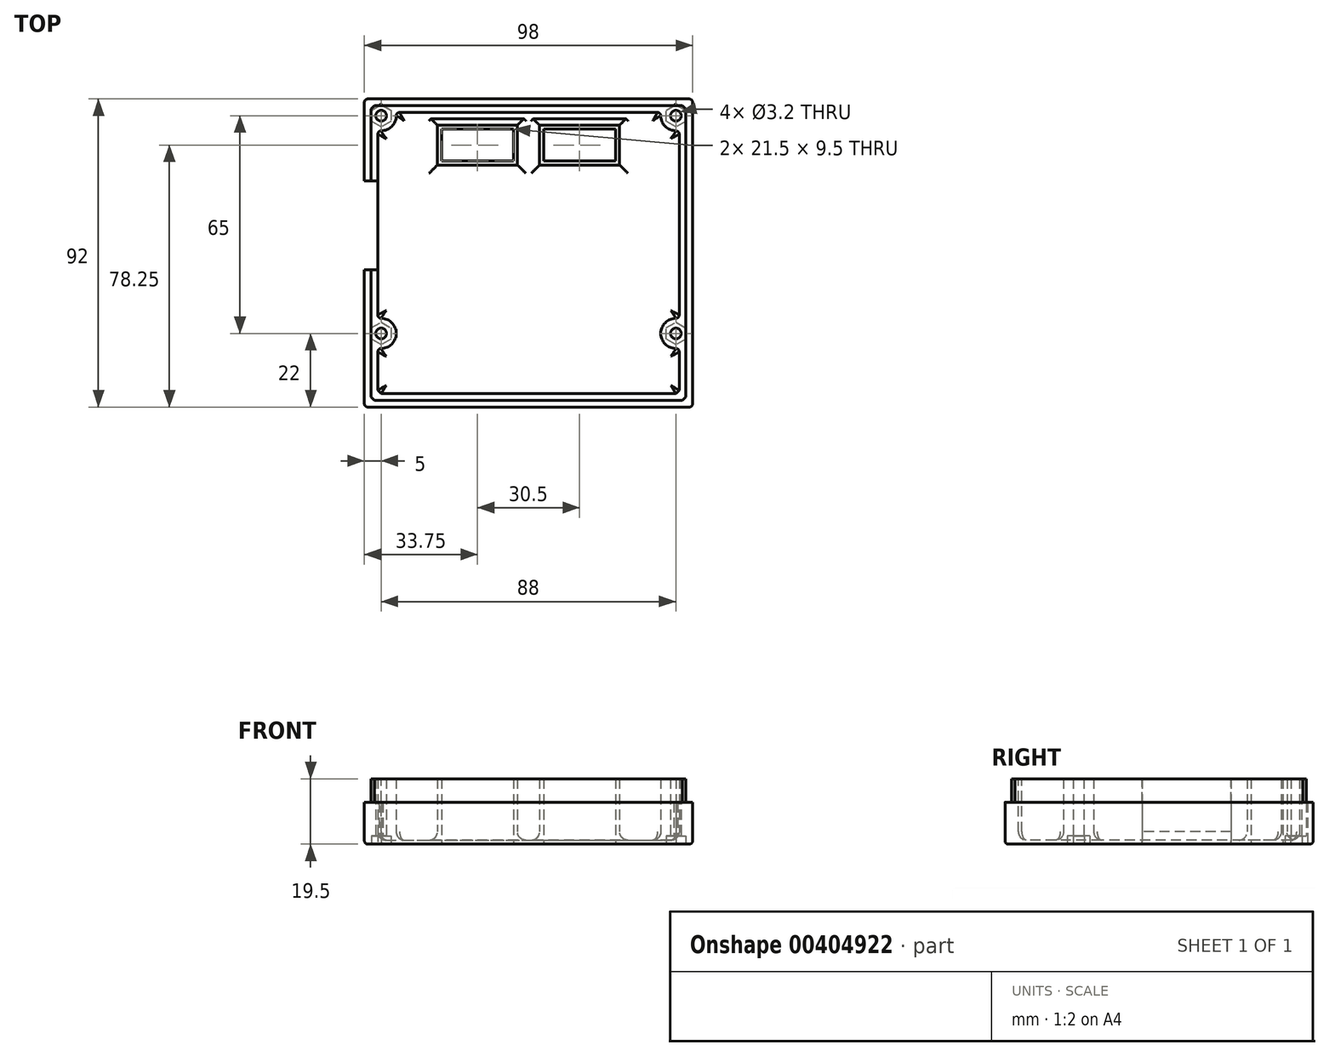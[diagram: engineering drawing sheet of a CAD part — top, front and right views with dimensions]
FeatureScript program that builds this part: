
annotation { "Feature Type Name" : "Feature", "Feature Type Description" : "" }
export const myFeature = defineFeature(function(context is Context, id is Id, definition is map)
    precondition{}
    {
        {
            var Q0;
            Q0=qCreatedBy(makeId("Top.planeOp"),FACE);
            var sketch = newSketch(context, id + "F0", { "sketchPlane" : qUnion([Q0])});
            skLineSegment(sketch, "E0.bottom", {"start": v(-47, 44) * mm, "end": v(47, 44) * mm});
            skLineSegment(sketch, "E0.top", {"start": v(-47, -44) * mm, "end": v(47, -44) * mm});
            skLineSegment(sketch, "E0.left", {"start": v(-47, 44) * mm, "end": v(-47, -44) * mm});
            skLineSegment(sketch, "E0.right", {"start": v(47, 44) * mm, "end": v(47, -44) * mm});
            skLineSegment(sketch, "E1.0", {"start": v(-49, 46) * mm, "end": v(49, 46) * mm});
            skLineSegment(sketch, "E1.1", {"start": v(-49, 46) * mm, "end": v(-49, -46) * mm});
            skLineSegment(sketch, "E1.2", {"start": v(-49, -46) * mm, "end": v(49, -46) * mm});
            skLineSegment(sketch, "E1.3", {"start": v(49, 46) * mm, "end": v(49, -46) * mm});
            skCircle(sketch, "E2", {"center": v(-44, 41) * mm, "radius": 1.6 * mm});
            skCircle(sketch, "E3", {"center": v(44, 41) * mm, "radius": 1.6 * mm});
            skCircle(sketch, "E4", {"center": v(-44, -24) * mm, "radius": 1.6 * mm});
            skCircle(sketch, "E5", {"center": v(44, -24) * mm, "radius": 1.6 * mm});
            skArc(sketch, "E6", {"start": v(-44, 36.5) * mm, "mid": v(-40.82, 37.82) * mm, "end": v(-39.5, 41) * mm});
            skArc(sketch, "E7", {"start": v(39.5, 41) * mm, "mid": v(40.82, 37.82) * mm, "end": v(44, 36.5) * mm});
            skArc(sketch, "E8", {"start": v(-44, -28.5) * mm, "mid": v(-39.5, -24) * mm, "end": v(-44, -19.5) * mm});
            skArc(sketch, "E9", {"start": v(44, -19.5) * mm, "mid": v(39.5, -24) * mm, "end": v(44, -28.5) * mm});
            skLineSegment(sketch, "E10", {"start": v(-49, 21.5) * mm, "end": v(-47, 21.5) * mm});
            skLineSegment(sketch, "E11", {"start": v(-49, -5) * mm, "end": v(-47, -5) * mm});
            skLineSegment(sketch, "E12.top", {"start": v(-45, -42) * mm, "end": v(45, -42) * mm});
            skLineSegment(sketch, "E12.left", {"start": v(-45, 35.5) * mm, "end": v(-45, -18.5) * mm});
            skLineSegment(sketch, "E12.right", {"start": v(45, 35.5) * mm, "end": v(45, -18.5) * mm});
            skLineSegment(sketch, "E13.trimOffspring", {"start": v(-45, -29.5) * mm, "end": v(-45, -42) * mm});
            skLineSegment(sketch, "E14.trimOffspring", {"start": v(45, -29.5) * mm, "end": v(45, -42) * mm});
            skArc(sketch, "E15.filletArc", {"start": v(45, -29.5) * mm, "mid": v(44.7, -28.8) * mm, "end": v(44, -28.5) * mm});
            skArc(sketch, "E16.filletArc", {"start": v(44, -19.5) * mm, "mid": v(44.7, -19.2) * mm, "end": v(45, -18.5) * mm});
            skArc(sketch, "E17.filletArc", {"start": v(-44, -28.5) * mm, "mid": v(-44.7, -28.8) * mm, "end": v(-45, -29.5) * mm});
            skArc(sketch, "E18.filletArc", {"start": v(-45, -18.5) * mm, "mid": v(-44.7, -19.2) * mm, "end": v(-44, -19.5) * mm});
            skLineSegment(sketch, "E19.trimOffspring", {"start": v(-38.5, 42) * mm, "end": v(38.5, 42) * mm});
            skArc(sketch, "E20.filletArc", {"start": v(-44, 36.5) * mm, "mid": v(-44.7, 36.2) * mm, "end": v(-45, 35.5) * mm});
            skArc(sketch, "E21.filletArc", {"start": v(-38.5, 42) * mm, "mid": v(-39.2, 41.7) * mm, "end": v(-39.5, 41) * mm});
            skPoint(sketch, "E22.visualSharp", {"position": v(39.61, 42) * mm});
            skArc(sketch, "E22.filletArc", {"start": v(39.5, 41) * mm, "mid": v(39.2, 41.7) * mm, "end": v(38.5, 42) * mm});
            skPoint(sketch, "E23.visualSharp", {"position": v(45, 36.61) * mm});
            skArc(sketch, "E23.filletArc", {"start": v(45, 35.5) * mm, "mid": v(44.7, 36.2) * mm, "end": v(44, 36.5) * mm});
            skLineSegment(sketch, "E24.bottom", {"start": v(-26, 37) * mm, "end": v(-4.5, 37) * mm});
            skLineSegment(sketch, "E24.top", {"start": v(-26, 27.5) * mm, "end": v(-4.5, 27.5) * mm});
            skLineSegment(sketch, "E24.left", {"start": v(-26, 37) * mm, "end": v(-26, 27.5) * mm});
            skLineSegment(sketch, "E24.right", {"start": v(-4.5, 37) * mm, "end": v(-4.5, 27.5) * mm});
            skLineSegment(sketch, "E25.bottom", {"start": v(4.5, 37) * mm, "end": v(26, 37) * mm});
            skLineSegment(sketch, "E25.top", {"start": v(4.5, 27.5) * mm, "end": v(26, 27.5) * mm});
            skLineSegment(sketch, "E25.left", {"start": v(4.5, 37) * mm, "end": v(4.5, 27.5) * mm});
            skLineSegment(sketch, "E25.right", {"start": v(26, 37) * mm, "end": v(26, 27.5) * mm});
            skCircle(sketch, "E26.cCircle", {"center": v(-44, 41) * mm, "radius": 2.9 * mm, "construction": true});
            skLineSegment(sketch, "E26.0", {"start": v(-46.9, 39.33) * mm, "end": v(-46.9, 42.67) * mm});
            skLineSegment(sketch, "E26.1", {"start": v(-46.9, 42.67) * mm, "end": v(-44, 44.35) * mm});
            skLineSegment(sketch, "E26.2", {"start": v(-44, 44.35) * mm, "end": v(-41.1, 42.67) * mm});
            skLineSegment(sketch, "E26.3", {"start": v(-41.1, 42.67) * mm, "end": v(-41.1, 39.33) * mm});
            skLineSegment(sketch, "E26.4", {"start": v(-41.1, 39.33) * mm, "end": v(-44, 37.65) * mm});
            skLineSegment(sketch, "E26.5", {"start": v(-44, 37.65) * mm, "end": v(-46.9, 39.33) * mm});
            skPoint(sketch, "E26.0.midPoint", {"position": v(-46.9, 41) * mm});
            skCircle(sketch, "E27.cCircle", {"center": v(44, 41) * mm, "radius": 2.9 * mm, "construction": true});
            skLineSegment(sketch, "E27.0", {"start": v(46.9, 42.67) * mm, "end": v(46.9, 39.33) * mm});
            skLineSegment(sketch, "E27.1", {"start": v(46.9, 39.33) * mm, "end": v(44, 37.65) * mm});
            skLineSegment(sketch, "E27.2", {"start": v(44, 37.65) * mm, "end": v(41.1, 39.33) * mm});
            skLineSegment(sketch, "E27.3", {"start": v(41.1, 39.33) * mm, "end": v(41.1, 42.67) * mm});
            skLineSegment(sketch, "E27.4", {"start": v(41.1, 42.67) * mm, "end": v(44, 44.35) * mm});
            skLineSegment(sketch, "E27.5", {"start": v(44, 44.35) * mm, "end": v(46.9, 42.67) * mm});
            skCircle(sketch, "E28.cCircle", {"center": v(-44, -24) * mm, "radius": 2.9 * mm, "construction": true});
            skLineSegment(sketch, "E28.0", {"start": v(-41.1, -22.33) * mm, "end": v(-41.1, -25.67) * mm});
            skLineSegment(sketch, "E28.1", {"start": v(-41.1, -25.67) * mm, "end": v(-44, -27.35) * mm});
            skLineSegment(sketch, "E28.2", {"start": v(-44, -27.35) * mm, "end": v(-46.9, -25.67) * mm});
            skLineSegment(sketch, "E28.3", {"start": v(-46.9, -25.67) * mm, "end": v(-46.9, -22.33) * mm});
            skLineSegment(sketch, "E28.4", {"start": v(-46.9, -22.33) * mm, "end": v(-44, -20.65) * mm});
            skLineSegment(sketch, "E28.5", {"start": v(-44, -20.65) * mm, "end": v(-41.1, -22.33) * mm});
            skPoint(sketch, "E28.0.midPoint", {"position": v(-41.1, -24) * mm});
            skCircle(sketch, "E29.cCircle", {"center": v(44, -24) * mm, "radius": 2.9 * mm, "construction": true});
            skLineSegment(sketch, "E29.0", {"start": v(46.9, -22.33) * mm, "end": v(46.9, -25.67) * mm});
            skLineSegment(sketch, "E29.1", {"start": v(46.9, -25.67) * mm, "end": v(44, -27.35) * mm});
            skLineSegment(sketch, "E29.2", {"start": v(44, -27.35) * mm, "end": v(41.1, -25.67) * mm});
            skLineSegment(sketch, "E29.3", {"start": v(41.1, -25.67) * mm, "end": v(41.1, -22.33) * mm});
            skLineSegment(sketch, "E29.4", {"start": v(41.1, -22.33) * mm, "end": v(44, -20.65) * mm});
            skLineSegment(sketch, "E29.5", {"start": v(44, -20.65) * mm, "end": v(46.9, -22.33) * mm});
            skPoint(sketch, "E29.0.midPoint", {"position": v(46.9, -24) * mm});
            skLineSegment(sketch, "E30.0", {"start": v(-27.2, 38.2) * mm, "end": v(-27.2, 26.3) * mm});
            skLineSegment(sketch, "E30.1", {"start": v(-27.2, 38.2) * mm, "end": v(-3.3, 38.2) * mm});
            skLineSegment(sketch, "E30.2", {"start": v(-3.3, 38.2) * mm, "end": v(-3.3, 26.3) * mm});
            skLineSegment(sketch, "E30.3", {"start": v(-27.2, 26.3) * mm, "end": v(-3.3, 26.3) * mm});
            skLineSegment(sketch, "E31.0", {"start": v(3.3, 38.2) * mm, "end": v(27.2, 38.2) * mm});
            skLineSegment(sketch, "E31.1", {"start": v(3.3, 38.2) * mm, "end": v(3.3, 26.3) * mm});
            skLineSegment(sketch, "E31.2", {"start": v(3.3, 26.3) * mm, "end": v(27.2, 26.3) * mm});
            skLineSegment(sketch, "E31.3", {"start": v(27.2, 38.2) * mm, "end": v(27.2, 26.3) * mm});
            skLineSegment(sketch, "E32", {"start": v(-47, -5) * mm, "end": v(-45, -5) * mm});
            skLineSegment(sketch, "E33", {"start": v(-47, 21.5) * mm, "end": v(-45, 21.5) * mm});
            skSolve(sketch);
        }
        {
            var Q0;
            Q0=makeQuery(id+"F0.imprint","IMPRINT",FACE,{"disambiguationData":[TD([[makeQuery(id+"F0.imprint","IMPRINT",EDGE,{"derivedFrom":sQuery(id+"F0.wireOp",EDGE,"E6")}),-1.0]])]});
            var Q1;
            Q1=makeQuery(id+"F0.imprint","IMPRINT",FACE,{"disambiguationData":[TD([[makeQuery(id+"F0.imprint","IMPRINT",EDGE,{"derivedFrom":sQuery(id+"F0.wireOp",EDGE,"E25.bottom")}),1.0]])]});
            var Q2;
            Q2=makeQuery(id+"F0.imprint","IMPRINT",FACE,{"disambiguationData":[TD([[makeQuery(id+"F0.imprint","IMPRINT",EDGE,{"derivedFrom":sQuery(id+"F0.wireOp",EDGE,"E24.bottom")}),1.0]])]});
            var Q3;
            {var subQ4=sQuery(id+"F0.wireOp",EDGE,"E0.top");Q3=makeQuery(id+"F0.imprint","IMPRINT",FACE,{"disambiguationData":[TD([[makeQuery(id+"F0.imprint","IMPRINT",EDGE,{"derivedFrom":subQ4}),-1.0]])]});}
            var Q4;
            Q4=makeQuery(id+"F0.imprint","IMPRINT",FACE,{"disambiguationData":[TD([[makeQuery(id+"F0.imprint","IMPRINT",EDGE,{"derivedFrom":sQuery(id+"F0.wireOp",EDGE,"feea0a20-fc6f-4da3-907b-8ab5c58ff8ee.0")}),-1.0]])]});
            var Q5;
            Q5=makeQuery(id+"F0.imprint","IMPRINT",FACE,{"disambiguationData":[TD([[makeQuery(id+"F0.imprint","IMPRINT",EDGE,{"derivedFrom":sQuery(id+"F0.wireOp",EDGE,"e97a09f4-8563-4df9-b0d7-211c7b4c223c")}),1.0]])]});
            var Q6;
            Q6=makeQuery(id+"F0.imprint","IMPRINT",FACE,{"disambiguationData":[TD([[makeQuery(id+"F0.imprint","IMPRINT",EDGE,{"derivedFrom":sQuery(id+"F0.wireOp",EDGE,"d8e0d119-aa0c-4ea7-b31c-518f6ddfd80a")}),1.0]])]});
            var Q7;
            Q7=makeQuery(id+"F0.imprint","IMPRINT",FACE,{"disambiguationData":[TD([[makeQuery(id+"F0.imprint","IMPRINT",EDGE,{"derivedFrom":sQuery(id+"F0.wireOp",EDGE,"f77a680e-791b-4a06-b991-cd855b51bd77.0")}),-1.0]])]});
            var Q8;
            {var subQ14=sQuery(id+"F0.wireOp",EDGE,"E0.top");Q8=makeQuery(id+"F0.imprint","IMPRINT",FACE,{"disambiguationData":[TD([[makeQuery(id+"F0.imprint","IMPRINT",EDGE,{"derivedFrom":subQ14}),1.0]])]});}
            var Q9;
            {var subQ0=sQuery(id+"F0.wireOp",EDGE,"E10");Q9=makeQuery(id+"F0.imprint","IMPRINT",FACE,{"disambiguationData":[TD([[makeQuery(id+"F0.imprint","IMPRINT",EDGE,{"derivedFrom":subQ0}),-1.0]])]});}
            var Q10;
            Q10=makeQuery(id+"F0.imprint","IMPRINT",FACE,{"disambiguationData":[TD([[makeQuery(id+"F0.imprint","IMPRINT",EDGE,{"derivedFrom":sQuery(id+"F0.wireOp",EDGE,"fc921a85-8c6c-4be7-88dc-233aecd465af")}),1.0]])]});
            var Q11;
            Q11=makeQuery(id+"F0.imprint","IMPRINT",FACE,{"disambiguationData":[TD([[makeQuery(id+"F0.imprint","IMPRINT",EDGE,{"derivedFrom":sQuery(id+"F0.wireOp",EDGE,"7167399d-95d6-4a2f-81b0-fee4431d182d.0")}),-1.0]])]});
            var Q12;
            {var subQ2=sQuery(id+"F0.wireOp",EDGE,"E32");Q12=makeQuery(id+"F0.imprint","IMPRINT",FACE,{"disambiguationData":[TD([[makeQuery(id+"F0.imprint","IMPRINT",EDGE,{"derivedFrom":subQ2}),1.0]])]});}
            extrude(context, id + "F1", {"entities" : qUnion([Q0, Q1, Q2, Q3, Q4, Q5, Q6, Q7, Q8, Q9, Q10, Q11, Q12]), "depth" : 1.2 * mm});
        }
        {
            var Q0;
            Q0=makeQuery(id+"F0.imprint","IMPRINT",FACE,{"disambiguationData":[TD([[makeQuery(id+"F0.imprint","IMPRINT",EDGE,{"derivedFrom":sQuery(id+"F0.wireOp",EDGE,"E24.bottom")}),1.0]])]});
            var Q1;
            Q1=makeQuery(id+"F0.imprint","IMPRINT",FACE,{"disambiguationData":[TD([[makeQuery(id+"F0.imprint","IMPRINT",EDGE,{"derivedFrom":sQuery(id+"F0.wireOp",EDGE,"E25.bottom")}),1.0]])]});
            var Q2;
            Q2=makeQuery(id+"F0.imprint","IMPRINT",FACE,{"disambiguationData":[TD([[makeQuery(id+"F0.imprint","IMPRINT",EDGE,{"derivedFrom":sQuery(id+"F0.wireOp",EDGE,"e97a09f4-8563-4df9-b0d7-211c7b4c223c")}),1.0]])]});
            var Q3;
            Q3=makeQuery(id+"F0.imprint","IMPRINT",FACE,{"disambiguationData":[TD([[makeQuery(id+"F0.imprint","IMPRINT",EDGE,{"derivedFrom":sQuery(id+"F0.wireOp",EDGE,"fc921a85-8c6c-4be7-88dc-233aecd465af")}),1.0]])]});
            var Q4;
            Q4=makeQuery(id+"F0.imprint","IMPRINT",FACE,{"disambiguationData":[TD([[makeQuery(id+"F0.imprint","IMPRINT",EDGE,{"derivedFrom":sQuery(id+"F0.wireOp",EDGE,"d8e0d119-aa0c-4ea7-b31c-518f6ddfd80a")}),1.0]])]});
            var Q5;
            {var subQ4=sQuery(id+"F0.wireOp",EDGE,"E0.top");Q5=makeQuery(id+"F0.imprint","IMPRINT",FACE,{"disambiguationData":[TD([[makeQuery(id+"F0.imprint","IMPRINT",EDGE,{"derivedFrom":subQ4}),-1.0]])]});}
            var Q6;
            {var subQ14=sQuery(id+"F0.wireOp",EDGE,"E0.top");Q6=makeQuery(id+"F0.imprint","IMPRINT",FACE,{"disambiguationData":[TD([[makeQuery(id+"F0.imprint","IMPRINT",EDGE,{"derivedFrom":subQ14}),1.0]])]});}
            var Q7;
            {var subQ0=sQuery(id+"F0.wireOp",EDGE,"E10");Q7=makeQuery(id+"F0.imprint","IMPRINT",FACE,{"disambiguationData":[TD([[makeQuery(id+"F0.imprint","IMPRINT",EDGE,{"derivedFrom":subQ0}),-1.0]])]});}
            var Q8;
            Q8=makeQuery(id+"F0.imprint","IMPRINT",FACE,{"disambiguationData":[TD([[makeQuery(id+"F0.imprint","IMPRINT",EDGE,{"derivedFrom":sQuery(id+"F0.wireOp",EDGE,"f77a680e-791b-4a06-b991-cd855b51bd77.0")}),-1.0]])]});
            var Q9;
            Q9=makeQuery(id+"F0.imprint","IMPRINT",FACE,{"disambiguationData":[TD([[makeQuery(id+"F0.imprint","IMPRINT",EDGE,{"derivedFrom":sQuery(id+"F0.wireOp",EDGE,"7167399d-95d6-4a2f-81b0-fee4431d182d.0")}),-1.0]])]});
            var Q10;
            Q10=makeQuery(id+"F0.imprint","IMPRINT",FACE,{"disambiguationData":[TD([[makeQuery(id+"F0.imprint","IMPRINT",EDGE,{"derivedFrom":sQuery(id+"F0.wireOp",EDGE,"feea0a20-fc6f-4da3-907b-8ab5c58ff8ee.0")}),-1.0]])]});
            var Q11;
            {var subQ2=sQuery(id+"F0.wireOp",EDGE,"E32");Q11=makeQuery(id+"F0.imprint","IMPRINT",FACE,{"disambiguationData":[TD([[makeQuery(id+"F0.imprint","IMPRINT",EDGE,{"derivedFrom":subQ2}),1.0]])]});}
            extrude(context, id + "F2", {"entities" : qUnion([Q0, Q1, Q2, Q3, Q4, Q5, Q6, Q7, Q8, Q9, Q10, Q11]), "operationType" : NewBodyOperationType.ADD, "depth" : 2.5 * mm, "hasSecondDirection" : true, "secondDirectionOppositeDirection" : false, "secondDirectionDepth" : 1.2 * mm});
        }
        {
            var Q0;
            {var subQ4=sQuery(id+"F0.wireOp",EDGE,"E0.top");Q0=makeQuery(id+"F0.imprint","IMPRINT",FACE,{"disambiguationData":[TD([[makeQuery(id+"F0.imprint","IMPRINT",EDGE,{"derivedFrom":subQ4}),-1.0]])]});}
            var Q1;
            {var subQ14=sQuery(id+"F0.wireOp",EDGE,"E0.top");Q1=makeQuery(id+"F0.imprint","IMPRINT",FACE,{"disambiguationData":[TD([[makeQuery(id+"F0.imprint","IMPRINT",EDGE,{"derivedFrom":subQ14}),1.0]])]});}
            var Q2;
            Q2=makeQuery(id+"F0.imprint","IMPRINT",FACE,{"disambiguationData":[TD([[makeQuery(id+"F0.imprint","IMPRINT",EDGE,{"derivedFrom":sQuery(id+"F0.wireOp",EDGE,"E4")}),-1.0]])]});
            var Q3;
            Q3=makeQuery(id+"F0.imprint","IMPRINT",FACE,{"disambiguationData":[TD([[makeQuery(id+"F0.imprint","IMPRINT",EDGE,{"derivedFrom":sQuery(id+"F0.wireOp",EDGE,"E5")}),-1.0]])]});
            var Q4;
            Q4=makeQuery(id+"F0.imprint","IMPRINT",FACE,{"disambiguationData":[TD([[makeQuery(id+"F0.imprint","IMPRINT",EDGE,{"derivedFrom":sQuery(id+"F0.wireOp",EDGE,"E3")}),-1.0]])]});
            var Q5;
            Q5=makeQuery(id+"F0.imprint","IMPRINT",FACE,{"disambiguationData":[TD([[makeQuery(id+"F0.imprint","IMPRINT",EDGE,{"derivedFrom":sQuery(id+"F0.wireOp",EDGE,"E2")}),-1.0]])]});
            var Q6;
            Q6=makeQuery(id+"F0.imprint","IMPRINT",FACE,{"disambiguationData":[TD([[makeQuery(id+"F0.imprint","IMPRINT",EDGE,{"derivedFrom":sQuery(id+"F0.wireOp",EDGE,"E24.bottom")}),1.0]])]});
            var Q7;
            Q7=makeQuery(id+"F0.imprint","IMPRINT",FACE,{"disambiguationData":[TD([[makeQuery(id+"F0.imprint","IMPRINT",EDGE,{"derivedFrom":sQuery(id+"F0.wireOp",EDGE,"E25.bottom")}),1.0]])]});
            var Q8;
            Q8=makeQuery(id+"F0.imprint","IMPRINT",FACE,{"disambiguationData":[TD([[makeQuery(id+"F0.imprint","IMPRINT",EDGE,{"derivedFrom":sQuery(id+"F0.wireOp",EDGE,"fc921a85-8c6c-4be7-88dc-233aecd465af")}),1.0]])]});
            var Q9;
            Q9=makeQuery(id+"F0.imprint","IMPRINT",FACE,{"disambiguationData":[TD([[makeQuery(id+"F0.imprint","IMPRINT",EDGE,{"derivedFrom":sQuery(id+"F0.wireOp",EDGE,"d8e0d119-aa0c-4ea7-b31c-518f6ddfd80a")}),1.0]])]});
            var Q10;
            Q10=makeQuery(id+"F0.imprint","IMPRINT",FACE,{"disambiguationData":[TD([[makeQuery(id+"F0.imprint","IMPRINT",EDGE,{"derivedFrom":sQuery(id+"F0.wireOp",EDGE,"e97a09f4-8563-4df9-b0d7-211c7b4c223c")}),1.0]])]});
            var Q11;
            {var subQ0=sQuery(id+"F0.wireOp",EDGE,"E10");Q11=makeQuery(id+"F0.imprint","IMPRINT",FACE,{"disambiguationData":[TD([[makeQuery(id+"F0.imprint","IMPRINT",EDGE,{"derivedFrom":subQ0}),-1.0]])]});}
            var Q12;
            {var subQ2=sQuery(id+"F0.wireOp",EDGE,"E32");Q12=makeQuery(id+"F0.imprint","IMPRINT",FACE,{"disambiguationData":[TD([[makeQuery(id+"F0.imprint","IMPRINT",EDGE,{"derivedFrom":subQ2}),1.0]])]});}
            var Q13;
            Q13=makeQuery(id+"F1.opExtrude","SWEPT_BODY",BODY,{"disambiguationData":[OSD([sQuery(id+"F0.wireOp",EDGE,"E1.0"),sQuery(id+"F0.wireOp",EDGE,"E1.1"),sQuery(id+"F0.wireOp",EDGE,"E1.2"),sQuery(id+"F0.wireOp",EDGE,"E1.3"),sQuery(id+"F0.wireOp",EDGE,"E24.bottom"),sQuery(id+"F0.wireOp",EDGE,"E24.top"),sQuery(id+"F0.wireOp",EDGE,"E24.left"),sQuery(id+"F0.wireOp",EDGE,"E24.right"),sQuery(id+"F0.wireOp",EDGE,"E25.bottom"),sQuery(id+"F0.wireOp",EDGE,"E25.top"),sQuery(id+"F0.wireOp",EDGE,"E25.left"),sQuery(id+"F0.wireOp",EDGE,"E25.right"),sQuery(id+"F0.wireOp",EDGE,"E26.0"),sQuery(id+"F0.wireOp",EDGE,"E26.1"),sQuery(id+"F0.wireOp",EDGE,"E26.2"),sQuery(id+"F0.wireOp",EDGE,"E26.3"),sQuery(id+"F0.wireOp",EDGE,"E26.4"),sQuery(id+"F0.wireOp",EDGE,"E26.5"),sQuery(id+"F0.wireOp",EDGE,"E27.0"),sQuery(id+"F0.wireOp",EDGE,"E27.1"),sQuery(id+"F0.wireOp",EDGE,"E27.2"),sQuery(id+"F0.wireOp",EDGE,"E27.3"),sQuery(id+"F0.wireOp",EDGE,"E27.4"),sQuery(id+"F0.wireOp",EDGE,"E27.5"),sQuery(id+"F0.wireOp",EDGE,"E28.0"),sQuery(id+"F0.wireOp",EDGE,"E28.1"),sQuery(id+"F0.wireOp",EDGE,"E28.2"),sQuery(id+"F0.wireOp",EDGE,"E28.3"),sQuery(id+"F0.wireOp",EDGE,"E28.4"),sQuery(id+"F0.wireOp",EDGE,"E28.5"),sQuery(id+"F0.wireOp",EDGE,"E29.0"),sQuery(id+"F0.wireOp",EDGE,"E29.1"),sQuery(id+"F0.wireOp",EDGE,"E29.2"),sQuery(id+"F0.wireOp",EDGE,"E29.3"),sQuery(id+"F0.wireOp",EDGE,"E29.4"),sQuery(id+"F0.wireOp",EDGE,"E29.5"),sQuery(id+"F0.wireOp",EDGE,"hLIKU86D-qEi8-tmS0-umkL-pXw8O5auwQbS"),sQuery(id+"F0.wireOp",EDGE,"S26CPWCd-tyL1-TwSH-uI1Q-NS7T4zvdQxxh"),sQuery(id+"F0.wireOp",EDGE,"bd91fcd1-0363-4304-9d41-4cc2dff9f5ec")])]});
            extrude(context, id + "F3", {"entities" : qUnion([Q0, Q1, Q2, Q3, Q4, Q5, Q6, Q7, Q8, Q9, Q10, Q11, Q12]), "operationType" : NewBodyOperationType.ADD, "depth" : 12.5 * mm, "hasSecondDirection" : true, "secondDirectionOppositeDirection" : false, "secondDirectionBoundEntityBody" : qUnion([Q13]), "secondDirectionDepth" : 2.5 * mm});
        }
        {
            var Q0;
            Q0=makeQuery(id+"F0.imprint","IMPRINT",FACE,{"disambiguationData":[TD([[makeQuery(id+"F0.imprint","IMPRINT",EDGE,{"derivedFrom":sQuery(id+"F0.wireOp",EDGE,"E24.bottom")}),1.0]])]});
            var Q1;
            Q1=makeQuery(id+"F0.imprint","IMPRINT",FACE,{"disambiguationData":[TD([[makeQuery(id+"F0.imprint","IMPRINT",EDGE,{"derivedFrom":sQuery(id+"F0.wireOp",EDGE,"E25.bottom")}),1.0]])]});
            var Q2;
            {var subQ14=sQuery(id+"F0.wireOp",EDGE,"E0.top");Q2=makeQuery(id+"F0.imprint","IMPRINT",FACE,{"disambiguationData":[TD([[makeQuery(id+"F0.imprint","IMPRINT",EDGE,{"derivedFrom":subQ14}),1.0]])]});}
            var Q3;
            Q3=makeQuery(id+"F0.imprint","IMPRINT",FACE,{"disambiguationData":[TD([[makeQuery(id+"F0.imprint","IMPRINT",EDGE,{"derivedFrom":sQuery(id+"F0.wireOp",EDGE,"fc921a85-8c6c-4be7-88dc-233aecd465af")}),1.0]])]});
            var Q4;
            Q4=makeQuery(id+"F0.imprint","IMPRINT",FACE,{"disambiguationData":[TD([[makeQuery(id+"F0.imprint","IMPRINT",EDGE,{"derivedFrom":sQuery(id+"F0.wireOp",EDGE,"d8e0d119-aa0c-4ea7-b31c-518f6ddfd80a")}),1.0]])]});
            var Q5;
            Q5=makeQuery(id+"F0.imprint","IMPRINT",FACE,{"disambiguationData":[TD([[makeQuery(id+"F0.imprint","IMPRINT",EDGE,{"derivedFrom":sQuery(id+"F0.wireOp",EDGE,"e97a09f4-8563-4df9-b0d7-211c7b4c223c")}),1.0]])]});
            var Q6;
            Q6=makeQuery(id+"F0.imprint","IMPRINT",FACE,{"disambiguationData":[TD([[makeQuery(id+"F0.imprint","IMPRINT",EDGE,{"derivedFrom":sQuery(id+"F0.wireOp",EDGE,"E4")}),-1.0]])]});
            var Q7;
            Q7=makeQuery(id+"F0.imprint","IMPRINT",FACE,{"disambiguationData":[TD([[makeQuery(id+"F0.imprint","IMPRINT",EDGE,{"derivedFrom":sQuery(id+"F0.wireOp",EDGE,"E5")}),-1.0]])]});
            var Q8;
            Q8=makeQuery(id+"F0.imprint","IMPRINT",FACE,{"disambiguationData":[TD([[makeQuery(id+"F0.imprint","IMPRINT",EDGE,{"derivedFrom":sQuery(id+"F0.wireOp",EDGE,"E3")}),-1.0]])]});
            var Q9;
            Q9=makeQuery(id+"F0.imprint","IMPRINT",FACE,{"disambiguationData":[TD([[makeQuery(id+"F0.imprint","IMPRINT",EDGE,{"derivedFrom":sQuery(id+"F0.wireOp",EDGE,"E2")}),-1.0]])]});
            var Q10;
            {var subQ2=sQuery(id+"F0.wireOp",EDGE,"E32");Q10=makeQuery(id+"F0.imprint","IMPRINT",FACE,{"disambiguationData":[TD([[makeQuery(id+"F0.imprint","IMPRINT",EDGE,{"derivedFrom":subQ2}),1.0]])]});}
            extrude(context, id + "F4", {"entities" : qUnion([Q0, Q1, Q2, Q3, Q4, Q5, Q6, Q7, Q8, Q9, Q10]), "operationType" : NewBodyOperationType.ADD, "depth" : 19.5 * mm, "hasSecondDirection" : true, "secondDirectionOppositeDirection" : false, "secondDirectionDepth" : 12.5 * mm});
        }
        {
            var Q0;
            {var subQ15=sQuery(id+"F0.wireOp",EDGE,"E0.top");Q0=makeQuery(id+"F0.imprint","IMPRINT",FACE,{"disambiguationData":[TD([[makeQuery(id+"F0.imprint","IMPRINT",EDGE,{"derivedFrom":subQ15}),1.0]])]});}
            var Q1;
            Q1=makeQuery(id+"F0.imprint","IMPRINT",FACE,{"disambiguationData":[TD([[makeQuery(id+"F0.imprint","IMPRINT",EDGE,{"derivedFrom":sQuery(id+"F0.wireOp",EDGE,"E2")}),-1.0]])]});
            var Q2;
            Q2=makeQuery(id+"F0.imprint","IMPRINT",FACE,{"disambiguationData":[TD([[makeQuery(id+"F0.imprint","IMPRINT",EDGE,{"derivedFrom":sQuery(id+"F0.wireOp",EDGE,"E3")}),-1.0]])]});
            var Q3;
            Q3=makeQuery(id+"F0.imprint","IMPRINT",FACE,{"disambiguationData":[TD([[makeQuery(id+"F0.imprint","IMPRINT",EDGE,{"derivedFrom":sQuery(id+"F0.wireOp",EDGE,"E5")}),-1.0]])]});
            var Q4;
            Q4=makeQuery(id+"F0.imprint","IMPRINT",FACE,{"disambiguationData":[TD([[makeQuery(id+"F0.imprint","IMPRINT",EDGE,{"derivedFrom":sQuery(id+"F0.wireOp",EDGE,"fc921a85-8c6c-4be7-88dc-233aecd465af")}),1.0]])]});
            var Q5;
            Q5=makeQuery(id+"F0.imprint","IMPRINT",FACE,{"disambiguationData":[TD([[makeQuery(id+"F0.imprint","IMPRINT",EDGE,{"derivedFrom":sQuery(id+"F0.wireOp",EDGE,"d8e0d119-aa0c-4ea7-b31c-518f6ddfd80a")}),1.0]])]});
            var Q6;
            Q6=makeQuery(id+"F0.imprint","IMPRINT",FACE,{"disambiguationData":[TD([[makeQuery(id+"F0.imprint","IMPRINT",EDGE,{"derivedFrom":sQuery(id+"F0.wireOp",EDGE,"e97a09f4-8563-4df9-b0d7-211c7b4c223c")}),1.0]])]});
            var Q7;
            Q7=makeQuery(id+"F0.imprint","IMPRINT",FACE,{"disambiguationData":[TD([[makeQuery(id+"F0.imprint","IMPRINT",EDGE,{"derivedFrom":sQuery(id+"F0.wireOp",EDGE,"E25.bottom")}),1.0]])]});
            var Q8;
            Q8=makeQuery(id+"F0.imprint","IMPRINT",FACE,{"disambiguationData":[TD([[makeQuery(id+"F0.imprint","IMPRINT",EDGE,{"derivedFrom":sQuery(id+"F0.wireOp",EDGE,"E24.bottom")}),1.0]])]});
            var Q9;
            Q9=makeQuery(id+"F0.imprint","IMPRINT",FACE,{"disambiguationData":[TD([[makeQuery(id+"F0.imprint","IMPRINT",EDGE,{"derivedFrom":sQuery(id+"F0.wireOp",EDGE,"E4")}),-1.0]])]});
            extrude(context, id + "F5", {"entities" : qUnion([Q0, Q1, Q2, Q3, Q4, Q5, Q6, Q7, Q8, Q9]), "operationType" : NewBodyOperationType.ADD, "depth" : 9 * mm, "hasSecondDirection" : true, "secondDirectionOppositeDirection" : false, "secondDirectionDepth" : 5.5 * mm});
        }
        {
            var Q0;
            Q0=makeQuery(id+"F1.opExtrude","CAP_FACE",FACE,{"disambiguationData":[OSD([sQuery(id+"F0.wireOp",EDGE,"E1.0"),sQuery(id+"F0.wireOp",EDGE,"E1.1"),sQuery(id+"F0.wireOp",EDGE,"E1.2"),sQuery(id+"F0.wireOp",EDGE,"E1.3"),sQuery(id+"F0.wireOp",EDGE,"E24.bottom"),sQuery(id+"F0.wireOp",EDGE,"E24.top"),sQuery(id+"F0.wireOp",EDGE,"E24.left"),sQuery(id+"F0.wireOp",EDGE,"E24.right"),sQuery(id+"F0.wireOp",EDGE,"E25.bottom"),sQuery(id+"F0.wireOp",EDGE,"E25.top"),sQuery(id+"F0.wireOp",EDGE,"E25.left"),sQuery(id+"F0.wireOp",EDGE,"E25.right"),sQuery(id+"F0.wireOp",EDGE,"E26.0"),sQuery(id+"F0.wireOp",EDGE,"E26.1"),sQuery(id+"F0.wireOp",EDGE,"E26.2"),sQuery(id+"F0.wireOp",EDGE,"E26.3"),sQuery(id+"F0.wireOp",EDGE,"E26.4"),sQuery(id+"F0.wireOp",EDGE,"E26.5"),sQuery(id+"F0.wireOp",EDGE,"E27.0"),sQuery(id+"F0.wireOp",EDGE,"E27.1"),sQuery(id+"F0.wireOp",EDGE,"E27.2"),sQuery(id+"F0.wireOp",EDGE,"E27.3"),sQuery(id+"F0.wireOp",EDGE,"E27.4"),sQuery(id+"F0.wireOp",EDGE,"E27.5"),sQuery(id+"F0.wireOp",EDGE,"E28.0"),sQuery(id+"F0.wireOp",EDGE,"E28.1"),sQuery(id+"F0.wireOp",EDGE,"E28.2"),sQuery(id+"F0.wireOp",EDGE,"E28.3"),sQuery(id+"F0.wireOp",EDGE,"E28.4"),sQuery(id+"F0.wireOp",EDGE,"E28.5"),sQuery(id+"F0.wireOp",EDGE,"E29.0"),sQuery(id+"F0.wireOp",EDGE,"E29.1"),sQuery(id+"F0.wireOp",EDGE,"E29.2"),sQuery(id+"F0.wireOp",EDGE,"E29.3"),sQuery(id+"F0.wireOp",EDGE,"E29.4"),sQuery(id+"F0.wireOp",EDGE,"E29.5"),sQuery(id+"F0.wireOp",EDGE,"hLIKU86D-qEi8-tmS0-umkL-pXw8O5auwQbS"),sQuery(id+"F0.wireOp",EDGE,"S26CPWCd-tyL1-TwSH-uI1Q-NS7T4zvdQxxh"),sQuery(id+"F0.wireOp",EDGE,"bd91fcd1-0363-4304-9d41-4cc2dff9f5ec")])],"isStart":false});
            fillet(context, id + "F6", {"entities" : qUnion([Q0]), "radius" : 2.5 * mm, "tangentPropagation" : true, "allowEdgeOverflow" : false});
        }
        {
            var Q0;
            Q0=makeQuery(id+"F5.opExtrude","CAP_EDGE",EDGE,{"disambiguationData":[OSD([sQuery(id+"F0.wireOp",EDGE,"E0.bottom")])],"isStart":false});
            var Q1;
            {var subQ0=sQuery(id+"F0.wireOp",EDGE,"E0.left");Q1=makeQuery(id+"F5.opExtrude","CAP_EDGE",EDGE,{"disambiguationData":[OSD([subQ0]),TDD([makeQuery(id+"F0.imprint","IMPRINT",EDGE,{"disambiguationData":[TD([[makeQuery(id+"F0.imprint","INTERSECT",VERTEX,{"derivedFrom":[sQuery(id+"F0.wireOp",EDGE,"E0.bottom"),subQ0]}),-1.0]])],"derivedFrom":subQ0})])],"isStart":false});}
            var Q2;
            {var subQ0=sQuery(id+"F0.wireOp",EDGE,"E0.left");Q2=makeQuery(id+"F5.opExtrude","CAP_EDGE",EDGE,{"disambiguationData":[OSD([subQ0]),TDD([makeQuery(id+"F0.imprint","IMPRINT",EDGE,{"disambiguationData":[TD([[makeQuery(id+"F0.imprint","INTERSECT",VERTEX,{"derivedFrom":[sQuery(id+"F0.wireOp",EDGE,"E0.top"),subQ0]}),1.0]])],"derivedFrom":subQ0})])],"isStart":false});}
            var Q3;
            Q3=makeQuery(id+"F5.opExtrude","CAP_EDGE",EDGE,{"disambiguationData":[OSD([sQuery(id+"F0.wireOp",EDGE,"E0.top")])],"isStart":false});
            var Q4;
            Q4=makeQuery(id+"F5.opExtrude","CAP_EDGE",EDGE,{"disambiguationData":[OSD([sQuery(id+"F0.wireOp",EDGE,"E0.right")])],"isStart":false});
            var Q5;
            {var subQ0=sQuery(id+"F0.wireOp",EDGE,"E0.left");var subQ1=sQuery(id+"F0.wireOp",EDGE,"E0.top");Q5=makeQuery(id+"F5.boolean.opBoolean","MERGE",EDGE,{"derivedFrom":[makeQuery(id+"F4.opExtrude","SWEPT_EDGE",EDGE,{"disambiguationData":[OSD([subQ1,subQ0])]}),makeQuery(id+"F5.opExtrude","SWEPT_EDGE",EDGE,{"disambiguationData":[OSD([subQ1,subQ0])]})]});}
            var Q6;
            {var subQ0=sQuery(id+"F0.wireOp",EDGE,"E0.right");var subQ1=sQuery(id+"F0.wireOp",EDGE,"E0.top");Q6=makeQuery(id+"F5.boolean.opBoolean","MERGE",EDGE,{"derivedFrom":[makeQuery(id+"F4.opExtrude","SWEPT_EDGE",EDGE,{"disambiguationData":[OSD([subQ1,subQ0])]}),makeQuery(id+"F5.opExtrude","SWEPT_EDGE",EDGE,{"disambiguationData":[OSD([subQ1,subQ0])]})]});}
            var Q7;
            {var subQ0=sQuery(id+"F0.wireOp",EDGE,"E0.right");var subQ1=sQuery(id+"F0.wireOp",EDGE,"E0.bottom");Q7=makeQuery(id+"F5.boolean.opBoolean","MERGE",EDGE,{"derivedFrom":[makeQuery(id+"F4.opExtrude","SWEPT_EDGE",EDGE,{"disambiguationData":[OSD([subQ1,subQ0])]}),makeQuery(id+"F5.opExtrude","SWEPT_EDGE",EDGE,{"disambiguationData":[OSD([subQ1,subQ0])]})]});}
            var Q8;
            {var subQ0=sQuery(id+"F0.wireOp",EDGE,"E0.left");var subQ1=sQuery(id+"F0.wireOp",EDGE,"E0.bottom");Q8=makeQuery(id+"F5.boolean.opBoolean","MERGE",EDGE,{"derivedFrom":[makeQuery(id+"F4.opExtrude","SWEPT_EDGE",EDGE,{"disambiguationData":[OSD([subQ1,subQ0])]}),makeQuery(id+"F5.opExtrude","SWEPT_EDGE",EDGE,{"disambiguationData":[OSD([subQ1,subQ0])]})]});}
            var Q9;
            {var subQ0=sQuery(id+"F0.wireOp",EDGE,"E14.trimOffspring");var subQ1=sQuery(id+"F0.wireOp",EDGE,"E12.top");Q9=makeQuery(id+"F5.boolean.opBoolean","MERGE",EDGE,{"derivedFrom":[makeQuery(id+"F4.boolean.opBoolean","MERGE",EDGE,{"derivedFrom":[makeQuery(id+"F3.boolean.opBoolean","MERGE",EDGE,{"derivedFrom":[makeQuery(id+"F2.opExtrude","SWEPT_EDGE",EDGE,{"disambiguationData":[OSD([subQ1,subQ0])]}),makeQuery(id+"F3.opExtrude","SWEPT_EDGE",EDGE,{"disambiguationData":[OSD([subQ1,subQ0])]})]}),makeQuery(id+"F4.opExtrude","SWEPT_EDGE",EDGE,{"disambiguationData":[OSD([subQ1,subQ0])]})]}),makeQuery(id+"F5.opExtrude","SWEPT_EDGE",EDGE,{"disambiguationData":[OSD([subQ1,subQ0])]})]});}
            var Q10;
            {var subQ0=sQuery(id+"F0.wireOp",EDGE,"E13.trimOffspring");var subQ1=sQuery(id+"F0.wireOp",EDGE,"E12.top");Q10=makeQuery(id+"F5.boolean.opBoolean","MERGE",EDGE,{"derivedFrom":[makeQuery(id+"F4.boolean.opBoolean","MERGE",EDGE,{"derivedFrom":[makeQuery(id+"F3.boolean.opBoolean","MERGE",EDGE,{"derivedFrom":[makeQuery(id+"F2.opExtrude","SWEPT_EDGE",EDGE,{"disambiguationData":[OSD([subQ1,subQ0])]}),makeQuery(id+"F3.opExtrude","SWEPT_EDGE",EDGE,{"disambiguationData":[OSD([subQ1,subQ0])]})]}),makeQuery(id+"F4.opExtrude","SWEPT_EDGE",EDGE,{"disambiguationData":[OSD([subQ1,subQ0])]})]}),makeQuery(id+"F5.opExtrude","SWEPT_EDGE",EDGE,{"disambiguationData":[OSD([subQ1,subQ0])]})]});}
            chamfer(context, id + "F7", {"entities" : qUnion([Q0, Q1, Q2, Q3, Q4, Q5, Q6, Q7, Q8, Q9, Q10]), "width" : 1 * mm, "tangentPropagation" : true});
        }
        {
            var Q0;
            {var subQ0=sQuery(id+"F0.wireOp",EDGE,"E1.3");var subQ1=sQuery(id+"F0.wireOp",EDGE,"E1.0");Q0=makeQuery(id+"F3.boolean.opBoolean","MERGE",EDGE,{"derivedFrom":[makeQuery(id+"F2.boolean.opBoolean","MERGE",EDGE,{"derivedFrom":[makeQuery(id+"F1.opExtrude","SWEPT_EDGE",EDGE,{"disambiguationData":[OSD([subQ1,subQ0])]}),makeQuery(id+"F2.opExtrude","SWEPT_EDGE",EDGE,{"disambiguationData":[OSD([subQ1,subQ0])]})]}),makeQuery(id+"F3.opExtrude","SWEPT_EDGE",EDGE,{"disambiguationData":[OSD([subQ1,subQ0])]})]});}
            var Q1;
            Q1=makeQuery(id+"F1.opExtrude","CAP_EDGE",EDGE,{"disambiguationData":[OSD([sQuery(id+"F0.wireOp",EDGE,"E1.0")])],"isStart":true});
            var Q2;
            {var subQ0=sQuery(id+"F0.wireOp",EDGE,"E1.1");var subQ1=sQuery(id+"F0.wireOp",EDGE,"E1.0");Q2=makeQuery(id+"F3.boolean.opBoolean","MERGE",EDGE,{"derivedFrom":[makeQuery(id+"F2.boolean.opBoolean","MERGE",EDGE,{"derivedFrom":[makeQuery(id+"F1.opExtrude","SWEPT_EDGE",EDGE,{"disambiguationData":[OSD([subQ1,subQ0])]}),makeQuery(id+"F2.opExtrude","SWEPT_EDGE",EDGE,{"disambiguationData":[OSD([subQ1,subQ0])]})]}),makeQuery(id+"F3.opExtrude","SWEPT_EDGE",EDGE,{"disambiguationData":[OSD([subQ1,subQ0])]})]});}
            var Q3;
            Q3=makeQuery(id+"F1.opExtrude","CAP_EDGE",EDGE,{"disambiguationData":[OSD([sQuery(id+"F0.wireOp",EDGE,"E1.1")])],"isStart":true});
            var Q4;
            {var subQ0=sQuery(id+"F0.wireOp",EDGE,"E1.2");var subQ1=sQuery(id+"F0.wireOp",EDGE,"E1.1");Q4=makeQuery(id+"F3.boolean.opBoolean","MERGE",EDGE,{"derivedFrom":[makeQuery(id+"F2.boolean.opBoolean","MERGE",EDGE,{"derivedFrom":[makeQuery(id+"F1.opExtrude","SWEPT_EDGE",EDGE,{"disambiguationData":[OSD([subQ1,subQ0])]}),makeQuery(id+"F2.opExtrude","SWEPT_EDGE",EDGE,{"disambiguationData":[OSD([subQ1,subQ0])]})]}),makeQuery(id+"F3.opExtrude","SWEPT_EDGE",EDGE,{"disambiguationData":[OSD([subQ1,subQ0])]})]});}
            var Q5;
            Q5=makeQuery(id+"F1.opExtrude","CAP_EDGE",EDGE,{"disambiguationData":[OSD([sQuery(id+"F0.wireOp",EDGE,"E1.2")])],"isStart":true});
            var Q6;
            {var subQ0=sQuery(id+"F0.wireOp",EDGE,"E1.3");var subQ1=sQuery(id+"F0.wireOp",EDGE,"E1.2");Q6=makeQuery(id+"F3.boolean.opBoolean","MERGE",EDGE,{"derivedFrom":[makeQuery(id+"F2.boolean.opBoolean","MERGE",EDGE,{"derivedFrom":[makeQuery(id+"F1.opExtrude","SWEPT_EDGE",EDGE,{"disambiguationData":[OSD([subQ1,subQ0])]}),makeQuery(id+"F2.opExtrude","SWEPT_EDGE",EDGE,{"disambiguationData":[OSD([subQ1,subQ0])]})]}),makeQuery(id+"F3.opExtrude","SWEPT_EDGE",EDGE,{"disambiguationData":[OSD([subQ1,subQ0])]})]});}
            var Q7;
            Q7=makeQuery(id+"F1.opExtrude","CAP_EDGE",EDGE,{"disambiguationData":[OSD([sQuery(id+"F0.wireOp",EDGE,"E1.3")])],"isStart":true});
            fillet(context, id + "F8", {"entities" : qUnion([Q0, Q1, Q2, Q3, Q4, Q5, Q6, Q7]), "radius" : 1 * mm, "tangentPropagation" : true, "allowEdgeOverflow" : false});
        }
        {
            var Q0;
            {var subQ2=sQuery(id+"F0.wireOp",EDGE,"E32");Q0=makeQuery(id+"F0.imprint","IMPRINT",FACE,{"disambiguationData":[TD([[makeQuery(id+"F0.imprint","IMPRINT",EDGE,{"derivedFrom":subQ2}),1.0]])]});}
            var Q1;
            {var subQ0=sQuery(id+"F0.wireOp",EDGE,"E10");Q1=makeQuery(id+"F0.imprint","IMPRINT",FACE,{"disambiguationData":[TD([[makeQuery(id+"F0.imprint","IMPRINT",EDGE,{"derivedFrom":subQ0}),-1.0]])]});}
            extrude(context, id + "F9", {"entities" : qUnion([Q0, Q1]), "operationType" : NewBodyOperationType.REMOVE, "depth" : 20 * mm, "hasSecondDirection" : true, "secondDirectionOppositeDirection" : true, "secondDirectionDepth" : 10 * mm});
        }
    });
